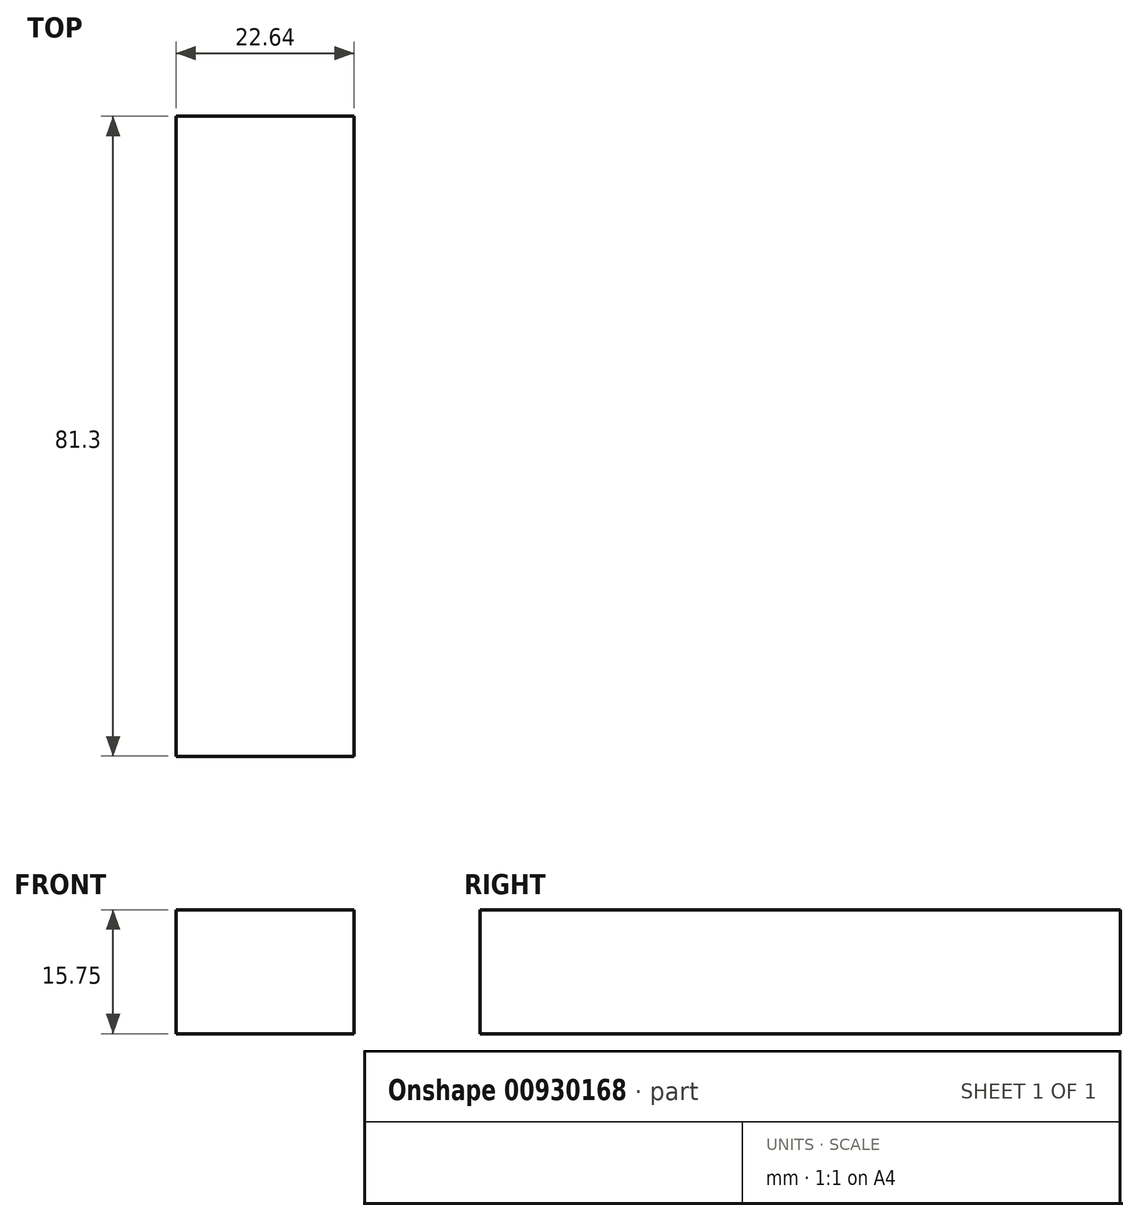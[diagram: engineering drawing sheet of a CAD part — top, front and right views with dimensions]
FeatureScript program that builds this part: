
annotation { "Feature Type Name" : "Feature", "Feature Type Description" : "" }
export const myFeature = defineFeature(function(context is Context, id is Id, definition is map)
    precondition{}
    {
        {
            var Q0;
            Q0=qCreatedBy(makeId("Top.planeOp"),FACE);
            var sketch = newSketch(context, id + "F0", { "sketchPlane" : qUnion([Q0])});
            skLineSegment(sketch, "E0", {"start": v(-122.24, -55.7) * mm, "end": v(-122.24, 25.61) * mm});
            skLineSegment(sketch, "E1", {"start": v(-122.24, 25.61) * mm, "end": v(-99.6, 25.61) * mm});
            skLineSegment(sketch, "E2", {"start": v(-99.6, 25.61) * mm, "end": v(-99.6, -55.7) * mm});
            skLineSegment(sketch, "E3", {"start": v(-99.6, -55.7) * mm, "end": v(-122.24, -55.7) * mm});
            skSolve(sketch);
        }
        {
            var Q0;
            Q0 = qSketchRegion(id + "F0", true);
            extrude(context, id + "F1", {"entities" : qUnion([Q0]), "depth" : 15.75 * mm, "offsetDistance" : 25.4 * mm});
        }
    });
